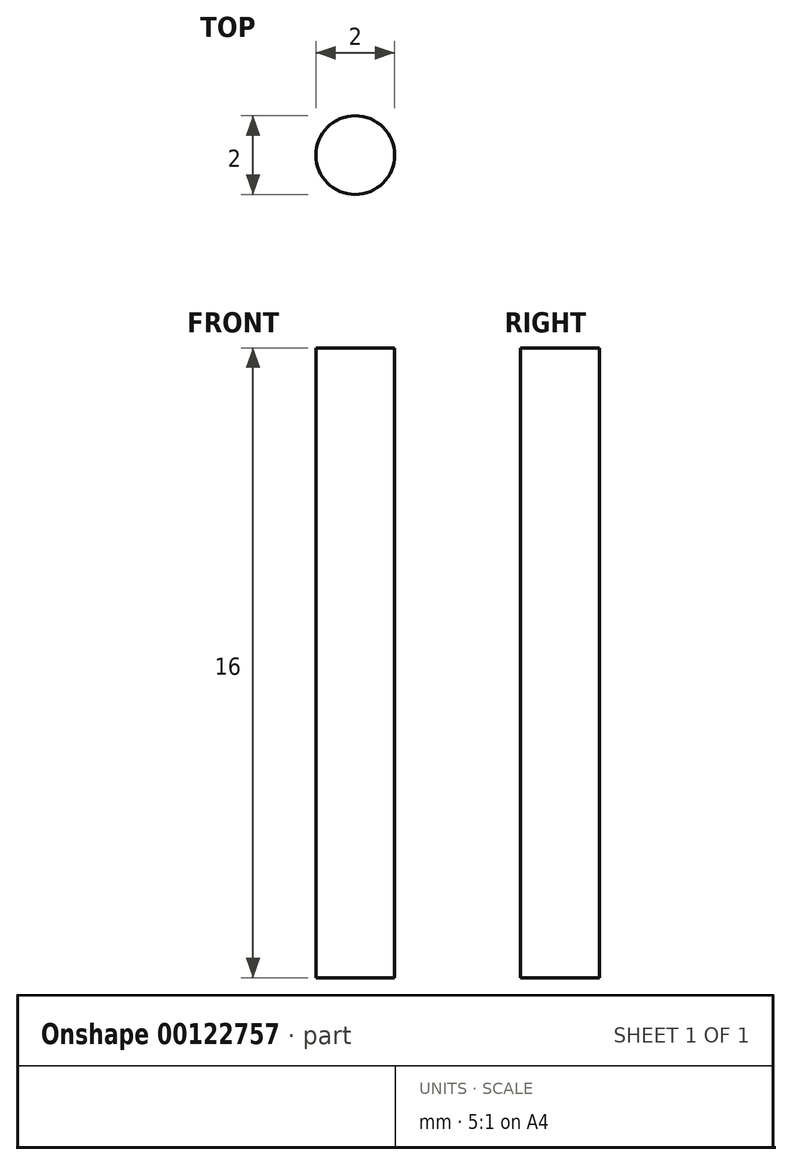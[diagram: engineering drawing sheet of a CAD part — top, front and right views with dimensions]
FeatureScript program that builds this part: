
annotation { "Feature Type Name" : "Feature", "Feature Type Description" : "" }
export const myFeature = defineFeature(function(context is Context, id is Id, definition is map)
    precondition{}
    {
        {
            var Q0;
            Q0=qCreatedBy(makeId("Top.planeOp"),FACE);
            var sketch = newSketch(context, id + "F0", { "sketchPlane" : qUnion([Q0])});
            skCircle(sketch, "E0", {"center": v(0, 0) * mm, "radius": 1 * mm});
            skSolve(sketch);
        }
        {
            var Q0;
            Q0=qSketchRegion(id+"F0",true);
            var Q1;
            Q1=makeQuery(id+"F0.imprint","IMPRINT",FACE,{"disambiguationData":[TD([[makeQuery(id+"F0.imprint","IMPRINT",EDGE,{"derivedFrom":sQuery(id+"F0.wireOp",EDGE,"E0")}),1.0]])]});
            extrude(context, id + "F1", {"entities" : qUnion([Q0, Q1]), "endBound" : BoundingType.SYMMETRIC, "depth" : 16 * mm});
        }
    });
